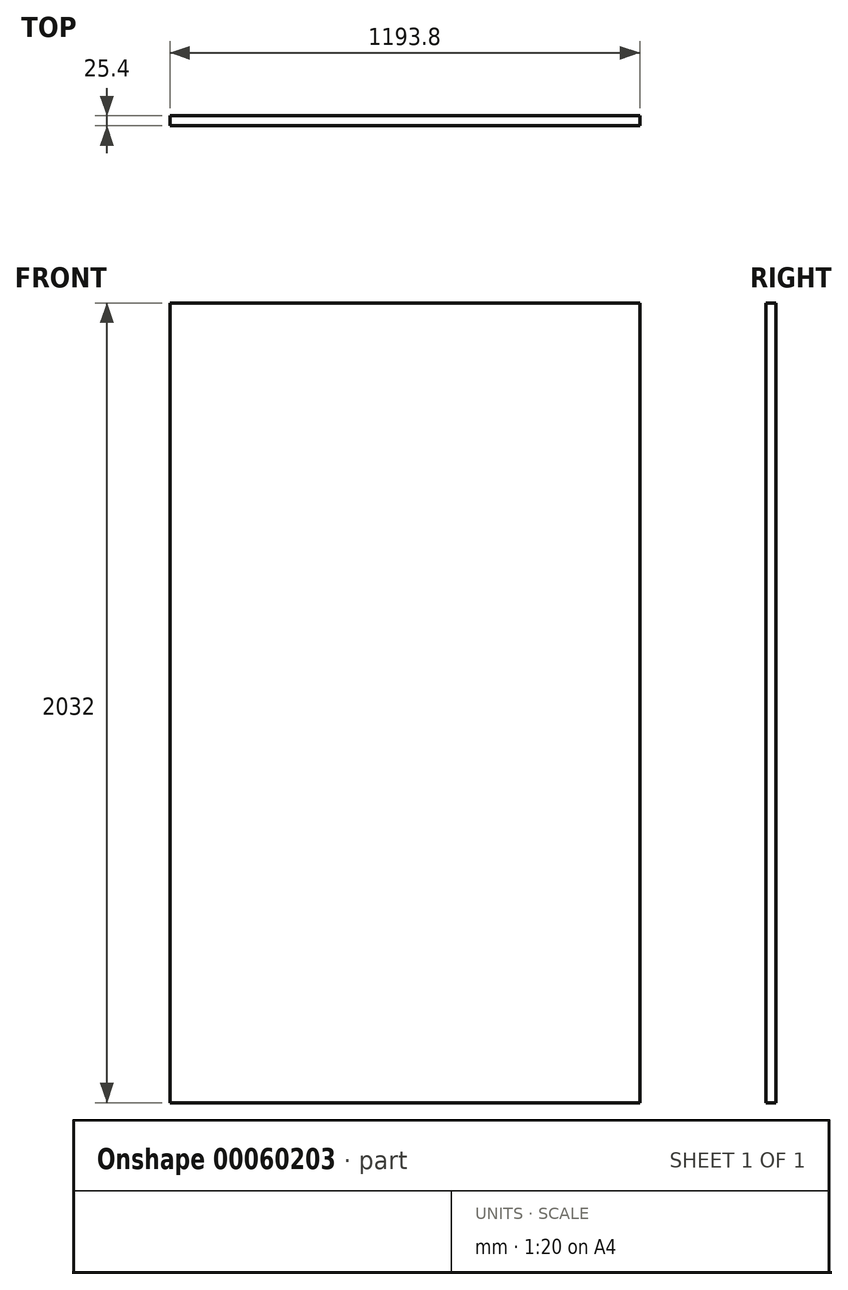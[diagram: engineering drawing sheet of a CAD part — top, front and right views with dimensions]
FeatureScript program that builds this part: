
annotation { "Feature Type Name" : "Feature", "Feature Type Description" : "" }
export const myFeature = defineFeature(function(context is Context, id is Id, definition is map)
    precondition{}
    {
        {
            var Q0;
            Q0=qCreatedBy(makeId("Front.planeOp"),FACE);
            var sketch = newSketch(context, id + "F0", { "sketchPlane" : qUnion([Q0])});
            skLineSegment(sketch, "E0.rect.bottom", {"start": v(596.9, 1016) * mm, "end": v(-596.9, 1016) * mm});
            skLineSegment(sketch, "E0.rect.top", {"start": v(596.9, -1016) * mm, "end": v(-596.9, -1016) * mm});
            skLineSegment(sketch, "E0.rect.left", {"start": v(596.9, 1016) * mm, "end": v(596.9, -1016) * mm});
            skLineSegment(sketch, "E0.rect.right", {"start": v(-596.9, 1016) * mm, "end": v(-596.9, -1016) * mm});
            skPoint(sketch, "E0.rect.middle", {"position": v(0, 0) * mm});
            skSolve(sketch);
        }
        {
            var Q0;
            Q0=makeQuery(id+"F0.imprint","IMPRINT",FACE,{"disambiguationData":[TD([[makeQuery(id+"F0.imprint","IMPRINT",EDGE,{"derivedFrom":sQuery(id+"F0.wireOp",EDGE,"E0.rect.bottom")}),1.0]])]});
            extrude(context, id + "F1", {"entities" : qUnion([Q0]), "depth" : 25.4 * mm});
        }
    });
